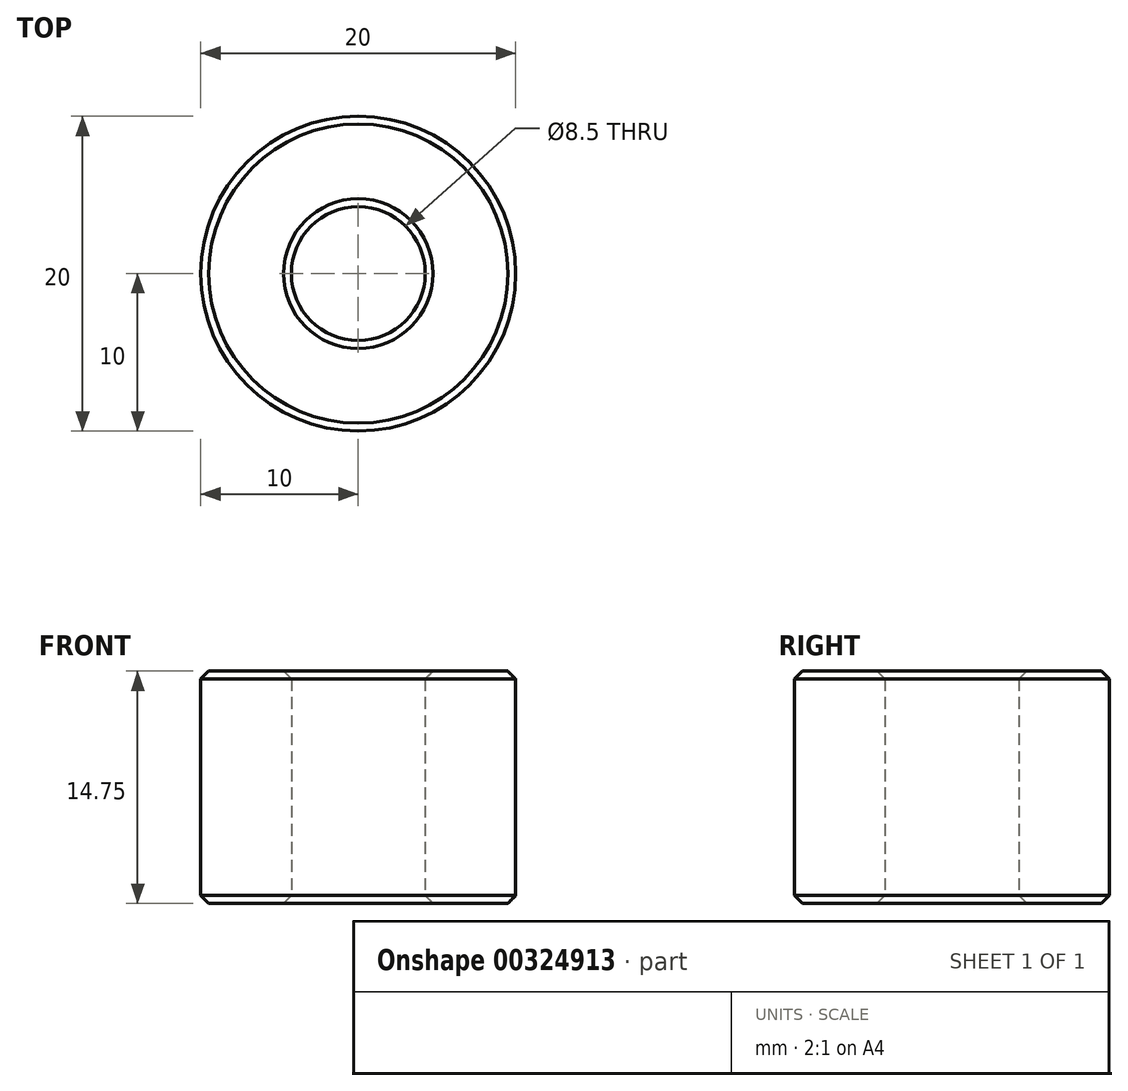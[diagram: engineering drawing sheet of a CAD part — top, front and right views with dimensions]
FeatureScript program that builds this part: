
annotation { "Feature Type Name" : "Feature", "Feature Type Description" : "" }
export const myFeature = defineFeature(function(context is Context, id is Id, definition is map)
    precondition{}
    {
        {
            var Q0;
            Q0=qCreatedBy(makeId("Top.planeOp"),FACE);
            var sketch = newSketch(context, id + "F0", { "sketchPlane" : qUnion([Q0])});
            skCircle(sketch, "E0", {"center": v(0, 0) * mm, "radius": 4.25 * mm});
            skCircle(sketch, "E1", {"center": v(0, 0) * mm, "radius": 10 * mm});
            skSolve(sketch);
        }
        {
            var Q0;
            Q0=makeQuery(id+"F0.imprint","IMPRINT",FACE,{"disambiguationData":[TD([[makeQuery(id+"F0.imprint","IMPRINT",EDGE,{"derivedFrom":sQuery(id+"F0.wireOp",EDGE,"E0")}),-1.0]])]});
            extrude(context, id + "F1", {"entities" : qUnion([Q0]), "depth" : 14.75 * mm});
        }
        {
            var Q0;
            Q0=makeQuery(id+"F1.opExtrude","CAP_FACE",FACE,{"disambiguationData":[OSD([sQuery(id+"F0.wireOp",EDGE,"E0"),sQuery(id+"F0.wireOp",EDGE,"E1")])],"isStart":false});
            var Q1;
            Q1=makeQuery(id+"F1.opExtrude","CAP_FACE",FACE,{"disambiguationData":[OSD([sQuery(id+"F0.wireOp",EDGE,"E0"),sQuery(id+"F0.wireOp",EDGE,"E1")])],"isStart":true});
            chamfer(context, id + "F2", {"entities" : qUnion([Q0, Q1]), "width" : 0.5 * mm, "tangentPropagation" : true});
        }
    });
